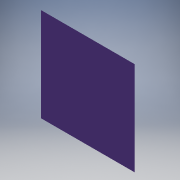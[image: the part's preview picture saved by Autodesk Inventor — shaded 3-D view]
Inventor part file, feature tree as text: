
AUTODESK INVENTOR PART (.ipt)
format: ipt  version: 2018 (Build 220112000, 112)  size: 95,744 bytes
history: native  units: mm
features: extrude x1, chamfer x1, sketch x1
ambient origin geometry x8: Origin, YZ Plane, XZ Plane, XY Plane, X Axis, Y Axis, Z Axis, Center Point
bodies: Volumenkörper1 (feature_tree)
feature tree (3):
  extrude  "Extrusion1"  Depth=20.0mm
  chamfer  "Fase1"  Distance=20.0mm
  sketch  "Skizze1"  dims[d0=440.0mm d1=440.0mm d2=20.0mm d3=0.0mm d4=20.0mm d5=2.0mm d6=45.0deg]
